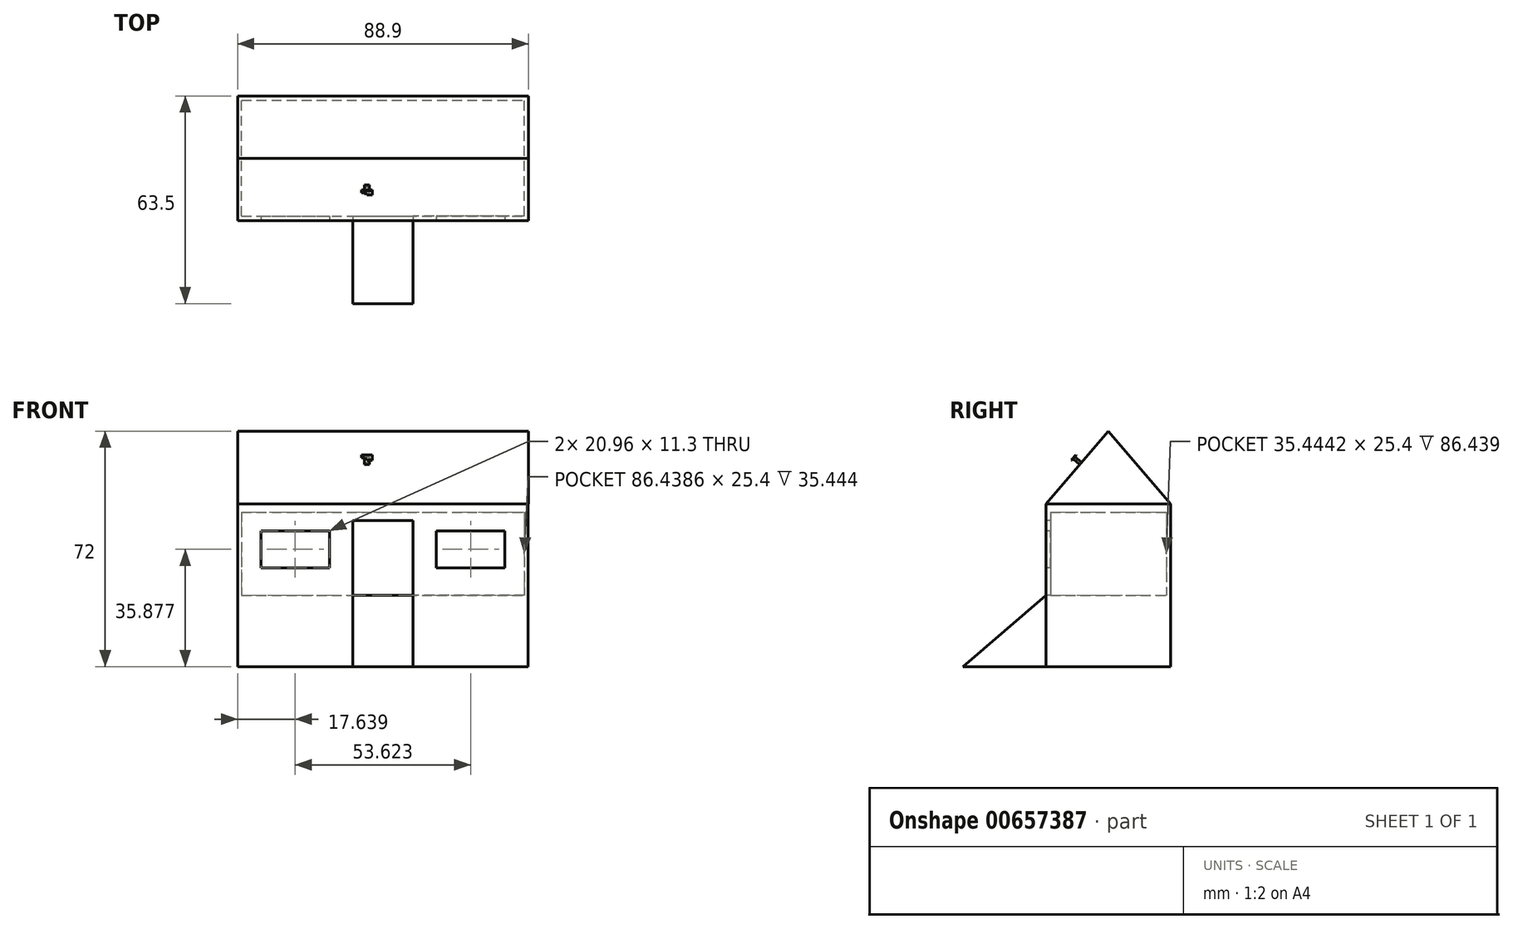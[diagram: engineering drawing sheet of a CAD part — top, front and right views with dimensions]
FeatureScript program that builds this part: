
annotation { "Feature Type Name" : "Feature", "Feature Type Description" : "" }
export const myFeature = defineFeature(function(context is Context, id is Id, definition is map)
    precondition{}
    {
        {
            var Q0;
            Q0=qCreatedBy(makeId("Front.planeOp"),FACE);
            var sketch = newSketch(context, id + "F0", { "sketchPlane" : qUnion([Q0])});
            skLineSegment(sketch, "E0", {"start": v(0, 0) * mm, "end": v(0, -14.47) * mm});
            skLineSegment(sketch, "E1", {"start": v(0, -14.47) * mm, "end": v(76.05, -14.47) * mm});
            skLineSegment(sketch, "E2.MirrorCS", {"start": v(0, -14.47) * mm, "end": v(-76.05, -14.47) * mm});
            skLineSegment(sketch, "E3", {"start": v(-44.34, -14.47) * mm, "end": v(-44.34, 0) * mm});
            skLineSegment(sketch, "E4", {"start": v(-44.34, 0) * mm, "end": v(0, 0) * mm});
            skLineSegment(sketch, "E5.MirrorCS", {"start": v(44.34, 0) * mm, "end": v(0, 0) * mm});
            skLineSegment(sketch, "E6.MirrorCS", {"start": v(44.34, -14.47) * mm, "end": v(44.34, 0) * mm});
            skLineSegment(sketch, "E7", {"start": v(-76.05, -14.47) * mm, "end": v(-76.05, -21.85) * mm});
            skLineSegment(sketch, "E8", {"start": v(-76.05, -21.85) * mm, "end": v(0, -21.85) * mm});
            skLineSegment(sketch, "E9", {"start": v(0, -21.85) * mm, "end": v(76.05, -21.85) * mm});
            skLineSegment(sketch, "E10", {"start": v(76.05, -21.85) * mm, "end": v(76.05, -14.47) * mm});
            skSolve(sketch);
        }
        {
            var Q0;
            Q0 = qSketchRegion(id + "F0", true);
            extrude(context, id + "F1", {"entities" : qUnion([Q0]), "depth" : 38.1 * mm, "offsetDistance" : 25.4 * mm});
        }
        {
            var Q0;
            Q0=makeQuery(id+"F1.opExtrude","SWEPT_FACE",FACE,{"disambiguationData":[OSD([sQuery(id+"F0.wireOp",EDGE,"E4"),sQuery(id+"F0.wireOp",EDGE,"E5.MirrorCS")])]});
            var sketch = newSketch(context, id + "F2", { "sketchPlane" : qUnion([Q0])});
            skLineSegment(sketch, "E11.0.0", {"start": v(44.34, 0) * mm, "end": v(-44.34, 0) * mm});
            skLineSegment(sketch, "E11.0.1", {"start": v(-44.34, 0) * mm, "end": v(-44.34, -38.1) * mm});
            skLineSegment(sketch, "E11.0.2", {"start": v(-44.34, -38.1) * mm, "end": v(44.34, -38.1) * mm});
            skLineSegment(sketch, "E11.0.3", {"start": v(44.34, -38.1) * mm, "end": v(44.34, 0) * mm});
            skLineSegment(sketch, "E12", {"start": v(-44.34, -36.68) * mm, "end": v(-9.2, -36.68) * mm});
            skLineSegment(sketch, "E13", {"start": v(-9.2, -36.68) * mm, "end": v(-9.2, -38.1) * mm});
            skLineSegment(sketch, "E14", {"start": v(-43.22, -36.68) * mm, "end": v(-43.22, 0) * mm});
            skLineSegment(sketch, "E15", {"start": v(-43.22, -1.24) * mm, "end": v(-9.2, -1.24) * mm});
            skLineSegment(sketch, "E16", {"start": v(-9.2, -1.24) * mm, "end": v(-9.2, 0) * mm});
            skLineSegment(sketch, "E17", {"start": v(0, 0) * mm, "end": v(0, -38.1) * mm, "construction": true});
            skLineSegment(sketch, "E18.MirrorCS", {"start": v(44.34, -36.68) * mm, "end": v(9.2, -36.68) * mm});
            skLineSegment(sketch, "E19.MirrorCS", {"start": v(9.2, -36.68) * mm, "end": v(9.2, -38.1) * mm});
            skLineSegment(sketch, "E20.MirrorCS", {"start": v(43.22, -36.68) * mm, "end": v(43.22, 0) * mm});
            skLineSegment(sketch, "E21.MirrorCS", {"start": v(43.22, -1.24) * mm, "end": v(9.2, -1.24) * mm});
            skLineSegment(sketch, "E22.MirrorCS", {"start": v(9.2, -1.24) * mm, "end": v(9.2, 0) * mm});
            skLineSegment(sketch, "E23", {"start": v(9.2, -1.24) * mm, "end": v(-9.2, -1.24) * mm});
            skLineSegment(sketch, "E24", {"start": v(-9.2, 0) * mm, "end": v(9.2, 0) * mm});
            skSolve(sketch);
        }
        {
            var Q0;
            {var subQ4=sQuery(id+"F2.wireOp",EDGE,"E15");Q0=makeQuery(id+"F2.imprint","IMPRINT",FACE,{"disambiguationData":[TD([[makeQuery(id+"F2.imprint","IMPRINT",EDGE,{"derivedFrom":subQ4}),1.0]])]});}
            var Q1;
            Q1=makeQuery(id+"F2.imprint","IMPRINT",FACE,{"disambiguationData":[TD([[makeQuery(id+"F2.imprint","IMPRINT",EDGE,{"derivedFrom":sQuery(id+"F2.wireOp",EDGE,"E16")}),-1.0]])]});
            var Q2;
            {var subQ4=sQuery(id+"F2.wireOp",EDGE,"E21.MirrorCS");Q2=makeQuery(id+"F2.imprint","IMPRINT",FACE,{"disambiguationData":[TD([[makeQuery(id+"F2.imprint","IMPRINT",EDGE,{"derivedFrom":subQ4}),-1.0]])]});}
            var Q3;
            {var subQ4=sQuery(id+"F2.wireOp",EDGE,"E11.0.1");var subQ5=sQuery(id+"F2.wireOp",EDGE,"E11.0.0");var subQ6=makeQuery(id+"F2.imprint","INTERSECT",VERTEX,{"derivedFrom":[subQ5,subQ4]});Q3=makeQuery(id+"F2.imprint","IMPRINT",FACE,{"disambiguationData":[TD([[makeQuery(id+"F2.imprint","IMPRINT",EDGE,{"disambiguationData":[TD([[subQ6,1.0]])],"derivedFrom":subQ5}),1.0]])]});}
            var Q4;
            {var subQ0=sQuery(id+"F2.wireOp",EDGE,"E13");Q4=makeQuery(id+"F2.imprint","IMPRINT",FACE,{"disambiguationData":[TD([[makeQuery(id+"F2.imprint","IMPRINT",EDGE,{"derivedFrom":subQ0}),-1.0]])]});}
            var Q5;
            {var subQ0=sQuery(id+"F2.wireOp",EDGE,"E19.MirrorCS");Q5=makeQuery(id+"F2.imprint","IMPRINT",FACE,{"disambiguationData":[TD([[makeQuery(id+"F2.imprint","IMPRINT",EDGE,{"derivedFrom":subQ0}),1.0]])]});}
            var Q6;
            {var subQ4=sQuery(id+"F2.wireOp",EDGE,"E11.0.3");var subQ5=sQuery(id+"F2.wireOp",EDGE,"E11.0.0");var subQ6=makeQuery(id+"F2.imprint","INTERSECT",VERTEX,{"derivedFrom":[subQ5,subQ4]});Q6=makeQuery(id+"F2.imprint","IMPRINT",FACE,{"disambiguationData":[TD([[makeQuery(id+"F2.imprint","IMPRINT",EDGE,{"disambiguationData":[TD([[subQ6,-1.0]])],"derivedFrom":subQ5}),1.0]])]});}
            extrude(context, id + "F3", {"entities" : qUnion([Q0, Q1, Q2, Q3, Q4, Q5, Q6]), "operationType" : NewBodyOperationType.ADD, "depth" : 25.4 * mm, "offsetDistance" : 25.4 * mm});
        }
        {
            var Q0;
            {var subQ0=sQuery(id+"F2.wireOp",EDGE,"E11.0.2");Q0=makeQuery(id+"F3.boolean.opBoolean","MERGE",FACE,{"derivedFrom":[makeQuery(id+"F1.opExtrude","CAP_FACE",FACE,{"disambiguationData":[OSD([sQuery(id+"F0.wireOp",EDGE,"E1"),sQuery(id+"F0.wireOp",EDGE,"E2.MirrorCS"),sQuery(id+"F0.wireOp",EDGE,"E3"),sQuery(id+"F0.wireOp",EDGE,"E4"),sQuery(id+"F0.wireOp",EDGE,"E5.MirrorCS"),sQuery(id+"F0.wireOp",EDGE,"E6.MirrorCS"),sQuery(id+"F0.wireOp",EDGE,"E7"),sQuery(id+"F0.wireOp",EDGE,"E8"),sQuery(id+"F0.wireOp",EDGE,"E9"),sQuery(id+"F0.wireOp",EDGE,"E10")])],"isStart":false}),makeQuery(id+"F3.opExtrude","SWEPT_FACE",FACE,{"disambiguationData":[OSD([subQ0]),TDD([makeQuery(id+"F2.imprint","IMPRINT",EDGE,{"disambiguationData":[TD([[makeQuery(id+"F2.imprint","INTERSECT",VERTEX,{"derivedFrom":[subQ0,sQuery(id+"F2.wireOp",EDGE,"E11.0.3")]}),-1.0]])],"derivedFrom":subQ0})])]}),makeQuery(id+"F3.opExtrude","SWEPT_FACE",FACE,{"disambiguationData":[OSD([subQ0]),TDD([makeQuery(id+"F2.imprint","IMPRINT",EDGE,{"disambiguationData":[TD([[makeQuery(id+"F2.imprint","INTERSECT",VERTEX,{"derivedFrom":[sQuery(id+"F2.wireOp",EDGE,"E11.0.1"),subQ0]}),1.0]])],"derivedFrom":subQ0})])]})]});}
            var sketch = newSketch(context, id + "F4", { "sketchPlane" : qUnion([Q0])});
            skLineSegment(sketch, "E25", {"start": v(0, 0) * mm, "end": v(0, 25.4) * mm, "construction": true});
            skLineSegment(sketch, "E26.0.0", {"start": v(44.34, -14.47) * mm, "end": v(44.34, 25.4) * mm});
            skLineSegment(sketch, "E26.0.1", {"start": v(44.34, 25.4) * mm, "end": v(9.2, 25.4) * mm});
            skLineSegment(sketch, "E26.0.2", {"start": v(9.2, 25.4) * mm, "end": v(9.2, 0) * mm});
            skLineSegment(sketch, "E26.0.3", {"start": v(9.2, 0) * mm, "end": v(-9.2, 0) * mm});
            skLineSegment(sketch, "E26.0.4", {"start": v(-9.2, 0) * mm, "end": v(-9.2, 25.4) * mm});
            skLineSegment(sketch, "E26.0.5", {"start": v(-9.2, 25.4) * mm, "end": v(-44.34, 25.4) * mm});
            skLineSegment(sketch, "E26.0.6", {"start": v(-44.34, 25.4) * mm, "end": v(-44.34, -14.47) * mm});
            skLineSegment(sketch, "E26.0.7", {"start": v(-44.34, -14.47) * mm, "end": v(-76.05, -14.47) * mm});
            skLineSegment(sketch, "E26.0.8", {"start": v(-76.05, -14.47) * mm, "end": v(-76.05, -21.85) * mm});
            skLineSegment(sketch, "E26.0.9", {"start": v(-76.05, -21.85) * mm, "end": v(76.05, -21.85) * mm});
            skLineSegment(sketch, "E26.0.10", {"start": v(76.05, -21.85) * mm, "end": v(76.05, -14.47) * mm});
            skLineSegment(sketch, "E26.0.11", {"start": v(76.05, -14.47) * mm, "end": v(44.34, -14.47) * mm});
            skLineSegment(sketch, "E27", {"start": v(-37.3, 19.68) * mm, "end": v(-37.3, 8.38) * mm});
            skLineSegment(sketch, "E28", {"start": v(-37.3, 8.38) * mm, "end": v(-16.33, 8.38) * mm});
            skLineSegment(sketch, "E29", {"start": v(-16.33, 8.38) * mm, "end": v(-16.33, 19.68) * mm});
            skLineSegment(sketch, "E30", {"start": v(-16.33, 19.68) * mm, "end": v(-37.3, 19.68) * mm});
            skLineSegment(sketch, "E31.MirrorCS", {"start": v(16.33, 8.38) * mm, "end": v(16.33, 19.68) * mm});
            skLineSegment(sketch, "E32.MirrorCS", {"start": v(16.33, 19.68) * mm, "end": v(37.3, 19.68) * mm});
            skLineSegment(sketch, "E33.MirrorCS", {"start": v(37.3, 8.38) * mm, "end": v(16.33, 8.38) * mm});
            skLineSegment(sketch, "E34.MirrorCS", {"start": v(37.3, 19.68) * mm, "end": v(37.3, 8.38) * mm});
            skSolve(sketch);
        }
        {
            var Q0;
            Q0=makeQuery(id+"F4.imprint","IMPRINT",FACE,{"disambiguationData":[TD([[makeQuery(id+"F4.imprint","IMPRINT",EDGE,{"derivedFrom":sQuery(id+"F4.wireOp",EDGE,"E27")}),1.0]])]});
            var Q1;
            Q1=makeQuery(id+"F4.imprint","IMPRINT",FACE,{"disambiguationData":[TD([[makeQuery(id+"F4.imprint","IMPRINT",EDGE,{"derivedFrom":sQuery(id+"F4.wireOp",EDGE,"E31.MirrorCS")}),-1.0]])]});
            extrude(context, id + "F5", {"entities" : qUnion([Q0, Q1]), "operationType" : NewBodyOperationType.REMOVE, "oppositeDirection" : true, "depth" : 25.4 * mm, "offsetDistance" : 25.4 * mm});
        }
        {
            var Q0;
            Q0=makeQuery(id+"F3.opExtrude","CAP_FACE",FACE,{"disambiguationData":[OSD([sQuery(id+"F2.wireOp",EDGE,"E11.0.0"),sQuery(id+"F2.wireOp",EDGE,"E11.0.1"),sQuery(id+"F2.wireOp",EDGE,"E11.0.2"),sQuery(id+"F2.wireOp",EDGE,"E11.0.3"),sQuery(id+"F2.wireOp",EDGE,"E12"),sQuery(id+"F2.wireOp",EDGE,"E13"),sQuery(id+"F2.wireOp",EDGE,"E14"),sQuery(id+"F2.wireOp",EDGE,"E15"),sQuery(id+"F2.wireOp",EDGE,"E19.MirrorCS"),sQuery(id+"F2.wireOp",EDGE,"E18.MirrorCS"),sQuery(id+"F2.wireOp",EDGE,"E20.MirrorCS"),sQuery(id+"F2.wireOp",EDGE,"E21.MirrorCS"),sQuery(id+"F2.wireOp",EDGE,"E23"),sQuery(id+"F2.wireOp",EDGE,"E24")])],"isStart":false});
            var sketch = newSketch(context, id + "F6", { "sketchPlane" : qUnion([Q0])});
            skLineSegment(sketch, "E35.0.0", {"start": v(-43.22, -1.24) * mm, "end": v(43.22, -1.24) * mm});
            skLineSegment(sketch, "E35.0.1", {"start": v(43.22, -1.24) * mm, "end": v(43.22, -36.68) * mm});
            skLineSegment(sketch, "E35.0.2", {"start": v(43.22, -36.68) * mm, "end": v(9.2, -36.68) * mm});
            skLineSegment(sketch, "E35.0.3", {"start": v(9.2, -36.68) * mm, "end": v(9.2, -38.1) * mm});
            skLineSegment(sketch, "E35.0.4", {"start": v(9.2, -38.1) * mm, "end": v(44.34, -38.1) * mm});
            skLineSegment(sketch, "E35.0.5", {"start": v(44.34, -38.1) * mm, "end": v(44.34, 0) * mm});
            skLineSegment(sketch, "E35.0.6", {"start": v(44.34, 0) * mm, "end": v(-44.34, 0) * mm});
            skLineSegment(sketch, "E35.0.7", {"start": v(-44.34, 0) * mm, "end": v(-44.34, -38.1) * mm});
            skLineSegment(sketch, "E35.0.8", {"start": v(-44.34, -38.1) * mm, "end": v(-9.2, -38.1) * mm});
            skLineSegment(sketch, "E35.0.9", {"start": v(-9.2, -38.1) * mm, "end": v(-9.2, -36.68) * mm});
            skLineSegment(sketch, "E35.0.10", {"start": v(-9.2, -36.68) * mm, "end": v(-43.22, -36.68) * mm});
            skLineSegment(sketch, "E35.0.11", {"start": v(-43.22, -36.68) * mm, "end": v(-43.22, -1.24) * mm});
            skLineSegment(sketch, "E36", {"start": v(-9.2, -38.1) * mm, "end": v(9.2, -38.1) * mm});
            skLineSegment(sketch, "E37", {"start": v(-9.2, -36.68) * mm, "end": v(9.2, -36.68) * mm});
            skSolve(sketch);
        }
        {
            var Q0;
            Q0=makeQuery(id+"F6.imprint","IMPRINT",FACE,{"disambiguationData":[TD([[makeQuery(id+"F6.imprint","IMPRINT",EDGE,{"derivedFrom":sQuery(id+"F6.wireOp",EDGE,"E35.0.3")}),-1.0]])]});
            extrude(context, id + "F7", {"entities" : qUnion([Q0]), "operationType" : NewBodyOperationType.ADD, "oppositeDirection" : true, "depth" : 2.54 * mm, "offsetDistance" : 25.4 * mm});
        }
        {
            var Q0;
            {var subQ0=sQuery(id+"F2.wireOp",EDGE,"E11.0.2");Q0=makeQuery(id+"F7.boolean.opBoolean","MERGE",FACE,{"derivedFrom":[makeQuery(id+"F3.boolean.opBoolean","MERGE",FACE,{"derivedFrom":[makeQuery(id+"F1.opExtrude","CAP_FACE",FACE,{"disambiguationData":[OSD([sQuery(id+"F0.wireOp",EDGE,"E1"),sQuery(id+"F0.wireOp",EDGE,"E2.MirrorCS"),sQuery(id+"F0.wireOp",EDGE,"E3"),sQuery(id+"F0.wireOp",EDGE,"E4"),sQuery(id+"F0.wireOp",EDGE,"E5.MirrorCS"),sQuery(id+"F0.wireOp",EDGE,"E6.MirrorCS"),sQuery(id+"F0.wireOp",EDGE,"E7"),sQuery(id+"F0.wireOp",EDGE,"E8"),sQuery(id+"F0.wireOp",EDGE,"E9"),sQuery(id+"F0.wireOp",EDGE,"E10")])],"isStart":false}),makeQuery(id+"F3.opExtrude","SWEPT_FACE",FACE,{"disambiguationData":[OSD([subQ0]),TDD([makeQuery(id+"F2.imprint","IMPRINT",EDGE,{"disambiguationData":[TD([[makeQuery(id+"F2.imprint","INTERSECT",VERTEX,{"derivedFrom":[subQ0,sQuery(id+"F2.wireOp",EDGE,"E11.0.3")]}),-1.0]])],"derivedFrom":subQ0})])]}),makeQuery(id+"F3.opExtrude","SWEPT_FACE",FACE,{"disambiguationData":[OSD([subQ0]),TDD([makeQuery(id+"F2.imprint","IMPRINT",EDGE,{"disambiguationData":[TD([[makeQuery(id+"F2.imprint","INTERSECT",VERTEX,{"derivedFrom":[sQuery(id+"F2.wireOp",EDGE,"E11.0.1"),subQ0]}),1.0]])],"derivedFrom":subQ0})])]})]}),makeQuery(id+"F7.opExtrude","SWEPT_FACE",FACE,{"disambiguationData":[OSD([sQuery(id+"F6.wireOp",EDGE,"E36")])]})]});}
            var sketch = newSketch(context, id + "F8", { "sketchPlane" : qUnion([Q0])});
            skLineSegment(sketch, "E38.0.0", {"start": v(44.34, -14.47) * mm, "end": v(44.34, 25.4) * mm});
            skLineSegment(sketch, "E38.0.1", {"start": v(44.34, 25.4) * mm, "end": v(-44.34, 25.4) * mm});
            skLineSegment(sketch, "E38.0.2", {"start": v(-44.34, 25.4) * mm, "end": v(-44.34, -14.47) * mm});
            skLineSegment(sketch, "E38.0.3", {"start": v(-44.34, -14.47) * mm, "end": v(-76.05, -14.47) * mm});
            skLineSegment(sketch, "E38.0.4", {"start": v(-76.05, -14.47) * mm, "end": v(-76.05, -21.85) * mm});
            skLineSegment(sketch, "E38.0.5", {"start": v(-76.05, -21.85) * mm, "end": v(76.05, -21.85) * mm});
            skLineSegment(sketch, "E38.0.6", {"start": v(76.05, -21.85) * mm, "end": v(76.05, -14.47) * mm});
            skLineSegment(sketch, "E38.0.7", {"start": v(76.05, -14.47) * mm, "end": v(44.34, -14.47) * mm});
            skLineSegment(sketch, "E39.bottom", {"start": v(-9.2, 0) * mm, "end": v(9.2, 0) * mm});
            skLineSegment(sketch, "E39.top", {"start": v(-9.2, -21.85) * mm, "end": v(9.2, -21.85) * mm});
            skLineSegment(sketch, "E39.left", {"start": v(-9.2, 0) * mm, "end": v(-9.2, -21.85) * mm});
            skLineSegment(sketch, "E39.right", {"start": v(9.2, 0) * mm, "end": v(9.2, -21.85) * mm});
            skSolve(sketch);
        }
        {
            var Q0;
            Q0=makeQuery(id+"F8.imprint","IMPRINT",FACE,{"disambiguationData":[TD([[makeQuery(id+"F8.imprint","IMPRINT",EDGE,{"derivedFrom":sQuery(id+"F8.wireOp",EDGE,"E39.bottom")}),1.0]])]});
            extrude(context, id + "F9", {"entities" : qUnion([Q0]), "operationType" : NewBodyOperationType.ADD, "depth" : 25.4 * mm, "offsetDistance" : 25.4 * mm});
        }
        {
            var Q0;
            Q0=makeQuery(id+"F9.opExtrude","SWEPT_FACE",FACE,{"disambiguationData":[OSD([sQuery(id+"F8.wireOp",EDGE,"E39.left")])]});
            var sketch = newSketch(context, id + "F10", { "sketchPlane" : qUnion([Q0])});
            skLineSegment(sketch, "E40.0.0", {"start": v(38.1, 0) * mm, "end": v(38.1, -21.85) * mm});
            skLineSegment(sketch, "E40.0.1", {"start": v(38.1, -21.85) * mm, "end": v(63.5, -21.85) * mm});
            skLineSegment(sketch, "E40.0.2", {"start": v(63.5, -21.85) * mm, "end": v(63.5, 0) * mm});
            skLineSegment(sketch, "E40.0.3", {"start": v(63.5, 0) * mm, "end": v(38.1, 0) * mm});
            skLineSegment(sketch, "E41", {"start": v(38.1, 0) * mm, "end": v(63.5, -21.85) * mm});
            skSolve(sketch);
        }
        {
            var Q0;
            Q0=makeQuery(id+"F10.imprint","IMPRINT",FACE,{"disambiguationData":[TD([[makeQuery(id+"F10.imprint","IMPRINT",EDGE,{"derivedFrom":sQuery(id+"F10.wireOp",EDGE,"E40.0.2")}),-1.0]])]});
            extrude(context, id + "F11", {"entities" : qUnion([Q0]), "operationType" : NewBodyOperationType.REMOVE, "oppositeDirection" : true, "depth" : 25.4 * mm, "offsetDistance" : 25.4 * mm});
        }
        {
            var Q0;
            Q0=makeQuery(id+"F7.boolean.opBoolean","MERGE",FACE,{"derivedFrom":[makeQuery(id+"F3.opExtrude","CAP_FACE",FACE,{"disambiguationData":[OSD([sQuery(id+"F2.wireOp",EDGE,"E11.0.0"),sQuery(id+"F2.wireOp",EDGE,"E11.0.1"),sQuery(id+"F2.wireOp",EDGE,"E11.0.2"),sQuery(id+"F2.wireOp",EDGE,"E11.0.3"),sQuery(id+"F2.wireOp",EDGE,"E12"),sQuery(id+"F2.wireOp",EDGE,"E13"),sQuery(id+"F2.wireOp",EDGE,"E14"),sQuery(id+"F2.wireOp",EDGE,"E15"),sQuery(id+"F2.wireOp",EDGE,"E19.MirrorCS"),sQuery(id+"F2.wireOp",EDGE,"E18.MirrorCS"),sQuery(id+"F2.wireOp",EDGE,"E20.MirrorCS"),sQuery(id+"F2.wireOp",EDGE,"E21.MirrorCS"),sQuery(id+"F2.wireOp",EDGE,"E23"),sQuery(id+"F2.wireOp",EDGE,"E24")])],"isStart":false}),makeQuery(id+"F7.opExtrude","CAP_FACE",FACE,{"disambiguationData":[OSD([sQuery(id+"F6.wireOp",EDGE,"E35.0.3"),sQuery(id+"F6.wireOp",EDGE,"E35.0.9"),sQuery(id+"F6.wireOp",EDGE,"E36"),sQuery(id+"F6.wireOp",EDGE,"E37")])],"isStart":true})]});
            var sketch = newSketch(context, id + "F12", { "sketchPlane" : qUnion([Q0])});
            skLineSegment(sketch, "E42.0.0", {"start": v(-44.34, 0) * mm, "end": v(-44.34, -38.1) * mm});
            skLineSegment(sketch, "E42.0.1", {"start": v(-44.34, -38.1) * mm, "end": v(44.34, -38.1) * mm});
            skLineSegment(sketch, "E42.0.2", {"start": v(44.34, -38.1) * mm, "end": v(44.34, 0) * mm});
            skLineSegment(sketch, "E42.0.3", {"start": v(44.34, 0) * mm, "end": v(-44.34, 0) * mm});
            skSolve(sketch);
        }
        {
            var Q0;
            Q0 = qSketchRegion(id + "F12", true);
            extrude(context, id + "F13", {"entities" : qUnion([Q0]), "operationType" : NewBodyOperationType.ADD, "depth" : 2.54 * mm, "offsetDistance" : 25.4 * mm});
        }
        {
            var Q0;
            Q0=qCreatedBy(makeId("Right.planeOp"),FACE);
            var sketch = newSketch(context, id + "F14", { "sketchPlane" : qUnion([Q0])});
            skLineSegment(sketch, "E43.0.0", {"start": v(0, -14.47) * mm, "end": v(0, 27.94) * mm});
            skLineSegment(sketch, "E43.0.1", {"start": v(0, 27.94) * mm, "end": v(-38.1, 27.94) * mm});
            skLineSegment(sketch, "E43.0.2", {"start": v(-38.1, 27.94) * mm, "end": v(-38.1, -14.47) * mm});
            skLineSegment(sketch, "E43.0.3", {"start": v(-38.1, -14.47) * mm, "end": v(0, -14.47) * mm});
            skLineSegment(sketch, "E44", {"start": v(-19.05, 27.94) * mm, "end": v(-19.05, 50.15) * mm});
            skLineSegment(sketch, "E45", {"start": v(-38.1, 27.94) * mm, "end": v(-19.05, 50.15) * mm});
            skLineSegment(sketch, "E46", {"start": v(-19.05, 50.15) * mm, "end": v(0, 27.94) * mm});
            skSolve(sketch);
        }
        {
            var Q0;
            {var subQ2=sQuery(id+"F14.wireOp",EDGE,"E44");Q0=makeQuery(id+"F14.imprint","IMPRINT",FACE,{"disambiguationData":[TD([[makeQuery(id+"F14.imprint","IMPRINT",EDGE,{"derivedFrom":subQ2}),1.0]])]});}
            var Q1;
            {var subQ2=sQuery(id+"F14.wireOp",EDGE,"E44");Q1=makeQuery(id+"F14.imprint","IMPRINT",FACE,{"disambiguationData":[TD([[makeQuery(id+"F14.imprint","IMPRINT",EDGE,{"derivedFrom":subQ2}),-1.0]])]});}
            extrude(context, id + "F15", {"entities" : qUnion([Q0, Q1]), "operationType" : NewBodyOperationType.ADD, "endBound" : BoundingType.SYMMETRIC, "depth" : 88.9 * mm, "offsetDistance" : 25.4 * mm});
        }
        {
            var Q0;
            Q0=makeQuery(id+"F1.opExtrude","SWEPT_FACE",FACE,{"disambiguationData":[OSD([sQuery(id+"F0.wireOp",EDGE,"E1")])]});
            var sketch = newSketch(context, id + "F16", { "sketchPlane" : qUnion([Q0])});
            skLineSegment(sketch, "E47.0.0", {"start": v(76.05, 0) * mm, "end": v(44.34, 0) * mm});
            skLineSegment(sketch, "E47.0.1", {"start": v(44.34, 0) * mm, "end": v(44.34, -38.1) * mm});
            skLineSegment(sketch, "E47.0.2", {"start": v(44.34, -38.1) * mm, "end": v(76.05, -38.1) * mm});
            skLineSegment(sketch, "E47.0.3", {"start": v(76.05, -38.1) * mm, "end": v(76.05, 0) * mm});
            skLineSegment(sketch, "E48.0.0", {"start": v(-44.34, 0) * mm, "end": v(-76.05, 0) * mm});
            skLineSegment(sketch, "E48.0.1", {"start": v(-76.05, 0) * mm, "end": v(-76.05, -38.1) * mm});
            skLineSegment(sketch, "E48.0.2", {"start": v(-76.05, -38.1) * mm, "end": v(-44.34, -38.1) * mm});
            skLineSegment(sketch, "E48.0.3", {"start": v(-44.34, -38.1) * mm, "end": v(-44.34, 0) * mm});
            skSolve(sketch);
        }
        {
            var Q0;
            Q0 = qSketchRegion(id + "F16", true);
            extrude(context, id + "F17", {"entities" : qUnion([Q0]), "operationType" : NewBodyOperationType.REMOVE, "oppositeDirection" : true, "depth" : 25.4 * mm, "offsetDistance" : 25.4 * mm});
        }
        {
            var Q0;
            Q0=makeQuery(id+"F15.opExtrude","SWEPT_FACE",FACE,{"disambiguationData":[OSD([sQuery(id+"F14.wireOp",EDGE,"E45")])]});
            var sketch = newSketch(context, id + "F18", { "sketchPlane" : qUnion([Q0])});
            skLineSegment(sketch, "E49.bottom", {"start": v(-5.69, 12.23) * mm, "end": v(-4.14, 12.23) * mm});
            skLineSegment(sketch, "E49.top", {"start": v(-5.69, 13.15) * mm, "end": v(-4.14, 13.15) * mm});
            skLineSegment(sketch, "E49.left", {"start": v(-5.69, 12.23) * mm, "end": v(-5.69, 13.15) * mm});
            skLineSegment(sketch, "E49.right", {"start": v(-4.14, 12.23) * mm, "end": v(-4.14, 13.15) * mm});
            skSolve(sketch);
        }
        {
            var Q0;
            Q0 = qSketchRegion(id + "F18", true);
            extrude(context, id + "F19", {"entities" : qUnion([Q0]), "operationType" : NewBodyOperationType.ADD, "depth" : 2.54 * mm, "offsetDistance" : 25.4 * mm});
        }
        {
            var Q0;
            Q0=makeQuery(id+"F19.opExtrude","CAP_FACE",FACE,{"disambiguationData":[OSD([sQuery(id+"F18.wireOp",EDGE,"E49.bottom"),sQuery(id+"F18.wireOp",EDGE,"E49.top"),sQuery(id+"F18.wireOp",EDGE,"E49.left"),sQuery(id+"F18.wireOp",EDGE,"E49.right")])],"isStart":false});
            var sketch = newSketch(context, id + "F20", { "sketchPlane" : qUnion([Q0])});
            skLineSegment(sketch, "E50.0.0", {"start": v(-4.14, 13.15) * mm, "end": v(-5.69, 13.15) * mm});
            skLineSegment(sketch, "E50.0.1", {"start": v(-5.69, 13.15) * mm, "end": v(-5.69, 12.23) * mm});
            skLineSegment(sketch, "E50.0.2", {"start": v(-5.69, 12.23) * mm, "end": v(-4.14, 12.23) * mm});
            skLineSegment(sketch, "E50.0.3", {"start": v(-4.14, 12.23) * mm, "end": v(-4.14, 13.15) * mm});
            skPoint(sketch, "E51.firstSnap0", {"position": v(-4.91, 12.23) * mm});
            skLineSegment(sketch, "E51.bottom", {"start": v(-4.91, 12.68) * mm, "end": v(-3.23, 12.68) * mm});
            skLineSegment(sketch, "E51.top", {"start": v(-4.91, 11.7) * mm, "end": v(-3.23, 11.7) * mm});
            skLineSegment(sketch, "E51.left", {"start": v(-4.91, 12.68) * mm, "end": v(-4.91, 11.7) * mm});
            skLineSegment(sketch, "E51.right", {"start": v(-3.23, 12.68) * mm, "end": v(-3.23, 11.7) * mm});
            skLineSegment(sketch, "E52", {"start": v(-4.91, 12.23) * mm, "end": v(-4.91, 13.15) * mm});
            skLineSegment(sketch, "E53", {"start": v(-4.91, 12.68) * mm, "end": v(-5.69, 12.68) * mm});
            skLineSegment(sketch, "E54.MirrorCS", {"start": v(-4.91, 13.67) * mm, "end": v(-3.23, 13.67) * mm});
            skLineSegment(sketch, "E55.MirrorCS", {"start": v(-3.23, 12.68) * mm, "end": v(-3.23, 13.67) * mm});
            skLineSegment(sketch, "E56.MirrorCS", {"start": v(-4.91, 12.68) * mm, "end": v(-4.91, 13.67) * mm});
            skLineSegment(sketch, "E57.MirrorCS", {"start": v(-4.91, 11.7) * mm, "end": v(-6.6, 11.7) * mm});
            skLineSegment(sketch, "E58.MirrorCS", {"start": v(-6.6, 12.68) * mm, "end": v(-6.6, 11.7) * mm});
            skLineSegment(sketch, "E59.MirrorCS", {"start": v(-6.6, 12.68) * mm, "end": v(-6.6, 13.67) * mm});
            skLineSegment(sketch, "E60.MirrorCS", {"start": v(-4.91, 13.67) * mm, "end": v(-6.6, 13.67) * mm});
            skLineSegment(sketch, "E61.MirrorCS", {"start": v(-4.91, 12.68) * mm, "end": v(-6.6, 12.68) * mm});
            skSolve(sketch);
        }
        {
            var Q0;
            {var subQ1=sQuery(id+"F20.wireOp",EDGE,"E59.MirrorCS");Q0=makeQuery(id+"F20.imprint","IMPRINT",FACE,{"disambiguationData":[TD([[makeQuery(id+"F20.imprint","IMPRINT",EDGE,{"derivedFrom":subQ1}),-1.0]])]});}
            var Q1;
            {var subQ4=sQuery(id+"F20.wireOp",EDGE,"E54.MirrorCS");Q1=makeQuery(id+"F20.imprint","IMPRINT",FACE,{"disambiguationData":[TD([[makeQuery(id+"F20.imprint","IMPRINT",EDGE,{"derivedFrom":subQ4}),-1.0]])]});}
            var Q2;
            Q2=makeQuery(id+"F20.imprint","IMPRINT",FACE,{"disambiguationData":[TD([[makeQuery(id+"F20.imprint","IMPRINT",EDGE,{"derivedFrom":sQuery(id+"F20.wireOp",EDGE,"E51.top")}),1.0]])]});
            var Q3;
            {var subQ0=sQuery(id+"F20.wireOp",EDGE,"E50.0.2");var subQ1=sQuery(id+"F20.wireOp",EDGE,"E50.0.1");var subQ2=makeQuery(id+"F20.imprint","INTERSECT",VERTEX,{"derivedFrom":[subQ1,subQ0]});Q3=makeQuery(id+"F20.imprint","IMPRINT",FACE,{"disambiguationData":[TD([[makeQuery(id+"F20.imprint","IMPRINT",EDGE,{"disambiguationData":[TD([[subQ2,-1.0]])],"derivedFrom":subQ1}),-1.0]])]});}
            var Q4;
            {var subQ0=sQuery(id+"F20.wireOp",EDGE,"E50.0.1");var subQ1=sQuery(id+"F20.wireOp",EDGE,"E50.0.0");var subQ2=makeQuery(id+"F20.imprint","INTERSECT",VERTEX,{"derivedFrom":[subQ1,subQ0]});Q4=makeQuery(id+"F20.imprint","IMPRINT",FACE,{"disambiguationData":[TD([[makeQuery(id+"F20.imprint","IMPRINT",EDGE,{"disambiguationData":[TD([[subQ2,-1.0]])],"derivedFrom":subQ1}),-1.0]])]});}
            var Q5;
            {var subQ0=sQuery(id+"F20.wireOp",EDGE,"E50.0.3");var subQ1=sQuery(id+"F20.wireOp",EDGE,"E50.0.0");var subQ2=makeQuery(id+"F20.imprint","INTERSECT",VERTEX,{"derivedFrom":[subQ1,subQ0]});Q5=makeQuery(id+"F20.imprint","IMPRINT",FACE,{"disambiguationData":[TD([[makeQuery(id+"F20.imprint","IMPRINT",EDGE,{"disambiguationData":[TD([[subQ2,1.0]])],"derivedFrom":subQ1}),-1.0]])]});}
            var Q6;
            {var subQ0=sQuery(id+"F20.wireOp",EDGE,"E50.0.3");var subQ1=sQuery(id+"F20.wireOp",EDGE,"E50.0.2");var subQ2=makeQuery(id+"F20.imprint","INTERSECT",VERTEX,{"derivedFrom":[subQ1,subQ0]});Q6=makeQuery(id+"F20.imprint","IMPRINT",FACE,{"disambiguationData":[TD([[makeQuery(id+"F20.imprint","IMPRINT",EDGE,{"disambiguationData":[TD([[subQ2,-1.0]])],"derivedFrom":subQ0}),1.0]])]});}
            var Q7;
            {var subQ0=sQuery(id+"F20.wireOp",EDGE,"E51.left");Q7=makeQuery(id+"F20.imprint","IMPRINT",FACE,{"disambiguationData":[TD([[makeQuery(id+"F20.imprint","IMPRINT",EDGE,{"derivedFrom":subQ0}),-1.0]])]});}
            extrude(context, id + "F21", {"entities" : qUnion([Q0, Q1, Q2, Q3, Q4, Q5, Q6, Q7]), "operationType" : NewBodyOperationType.ADD, "depth" : 0.25 * mm, "offsetDistance" : 25.4 * mm});
        }
    });
